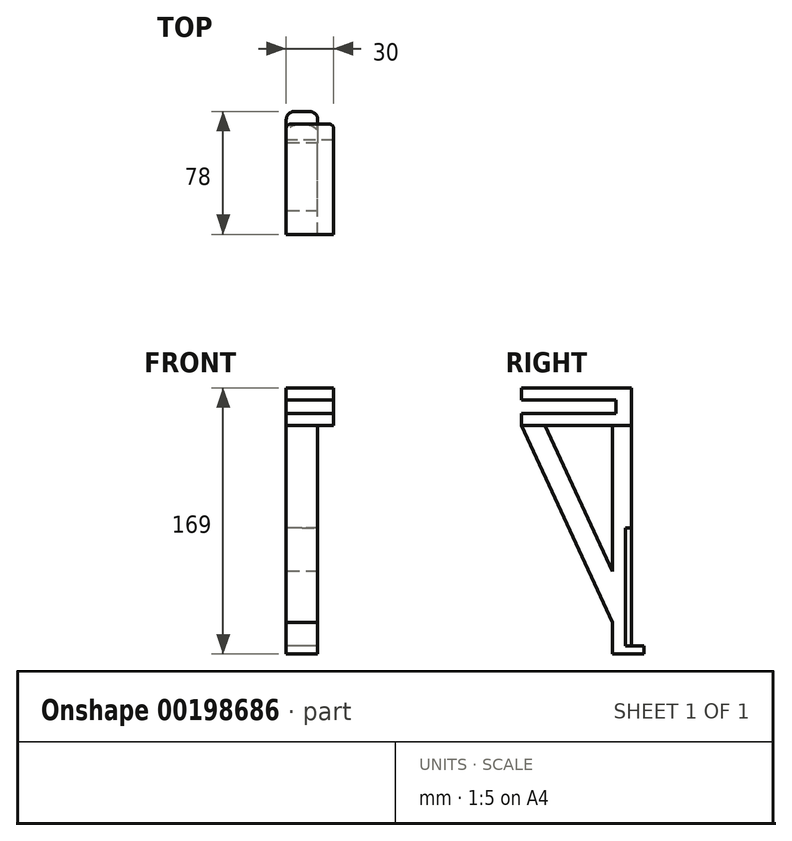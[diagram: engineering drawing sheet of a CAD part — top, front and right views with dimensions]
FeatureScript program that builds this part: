
annotation { "Feature Type Name" : "Feature", "Feature Type Description" : "" }
export const myFeature = defineFeature(function(context is Context, id is Id, definition is map)
    precondition{}
    {
        {
            var Q0;
            Q0=qCreatedBy(makeId("Top.planeOp"),FACE);
            var sketch = newSketch(context, id + "F0", { "sketchPlane" : qUnion([Q0])});
            skLineSegment(sketch, "E0.bottom", {"start": v(0, 0) * mm, "end": v(30, 0) * mm});
            skLineSegment(sketch, "E0.top", {"start": v(0, -70) * mm, "end": v(30, -70) * mm});
            skLineSegment(sketch, "E0.left", {"start": v(0, 0) * mm, "end": v(0, -70) * mm});
            skLineSegment(sketch, "E0.right", {"start": v(30, 0) * mm, "end": v(30, -70) * mm});
            skSolve(sketch);
        }
        {
            var Q0;
            Q0=makeQuery(id+"F0.imprint","IMPRINT",FACE,{"disambiguationData":[TD([[makeQuery(id+"F0.imprint","IMPRINT",EDGE,{"derivedFrom":sQuery(id+"F0.wireOp",EDGE,"E0.bottom")}),-1.0]])]});
            extrude(context, id + "F1", {"entities" : qUnion([Q0]), "depth" : 24 * mm});
        }
        {
            var Q0;
            Q0=makeQuery(id+"F1.opExtrude","SWEPT_FACE",FACE,{"disambiguationData":[OSD([sQuery(id+"F0.wireOp",EDGE,"E0.left")])]});
            var sketch = newSketch(context, id + "F2", { "sketchPlane" : qUnion([Q0])});
            skLineSegment(sketch, "E1.bottom", {"start": v(70, 7.9) * mm, "end": v(10, 7.9) * mm});
            skLineSegment(sketch, "E1.top", {"start": v(70, 16.3) * mm, "end": v(10, 16.3) * mm});
            skLineSegment(sketch, "E1.left", {"start": v(70, 7.9) * mm, "end": v(70, 16.3) * mm});
            skLineSegment(sketch, "E1.right", {"start": v(10, 7.9) * mm, "end": v(10, 16.3) * mm});
            skSolve(sketch);
        }
        {
            var Q0;
            Q0=makeQuery(id+"F2.imprint","IMPRINT",FACE,{"disambiguationData":[TD([[makeQuery(id+"F2.imprint","IMPRINT",EDGE,{"derivedFrom":sQuery(id+"F2.wireOp",EDGE,"E1.bottom")}),-1.0]])]});
            extrude(context, id + "F3", {"entities" : qUnion([Q0]), "operationType" : NewBodyOperationType.REMOVE, "endBound" : BoundingType.THROUGH_ALL, "oppositeDirection" : true, "depth" : 25 * mm});
        }
        {
            var Q0;
            Q0=qCreatedBy(makeId("Right.planeOp"),FACE);
            var sketch = newSketch(context, id + "F4", { "sketchPlane" : qUnion([Q0])});
            skLineSegment(sketch, "E2.bottom", {"start": v(0, 0) * mm, "end": v(-12, 0) * mm});
            skLineSegment(sketch, "E2.top", {"start": v(0, -145) * mm, "end": v(-12, -145) * mm});
            skLineSegment(sketch, "E2.left", {"start": v(0, 0) * mm, "end": v(0, -145) * mm});
            skLineSegment(sketch, "E2.right", {"start": v(-12, 0) * mm, "end": v(-12, -145) * mm});
            skLineSegment(sketch, "E3", {"start": v(-70, 0) * mm, "end": v(-55, 0) * mm});
            skLineSegment(sketch, "E4", {"start": v(-55, 0) * mm, "end": v(-12, -92.67) * mm});
            skLineSegment(sketch, "E5", {"start": v(-70, 0) * mm, "end": v(-12, -125) * mm});
            skSolve(sketch);
        }
        {
            var Q0;
            {var subQ1=sQuery(id+"F4.wireOp",EDGE,"E2.bottom");Q0=makeQuery(id+"F4.imprint","IMPRINT",FACE,{"disambiguationData":[TD([[makeQuery(id+"F4.imprint","IMPRINT",EDGE,{"derivedFrom":subQ1}),1.0]])]});}
            var Q1;
            Q1=makeQuery(id+"F4.imprint","IMPRINT",FACE,{"disambiguationData":[TD([[makeQuery(id+"F4.imprint","IMPRINT",EDGE,{"derivedFrom":sQuery(id+"F4.wireOp",EDGE,"E3")}),-1.0]])]});
            extrude(context, id + "F5", {"entities" : qUnion([Q0, Q1]), "operationType" : NewBodyOperationType.ADD, "depth" : 20 * mm});
        }
        {
            var Q0;
            Q0=makeQuery(id+"F5.boolean.opBoolean","MERGE",FACE,{"derivedFrom":[makeQuery(id+"F1.opExtrude","SWEPT_FACE",FACE,{"disambiguationData":[OSD([sQuery(id+"F0.wireOp",EDGE,"E0.bottom")])]}),makeQuery(id+"F5.opExtrude","SWEPT_FACE",FACE,{"disambiguationData":[OSD([sQuery(id+"F4.wireOp",EDGE,"E2.left")])]})]});
            var sketch = newSketch(context, id + "F6", { "sketchPlane" : qUnion([Q0])});
            skLineSegment(sketch, "E6.bottom", {"start": v(-20, -145) * mm, "end": v(0, -145) * mm});
            skLineSegment(sketch, "E6.top", {"start": v(-20, -140) * mm, "end": v(0, -140) * mm});
            skLineSegment(sketch, "E6.left", {"start": v(-20, -145) * mm, "end": v(-20, -140) * mm});
            skLineSegment(sketch, "E6.right", {"start": v(0, -145) * mm, "end": v(0, -140) * mm});
            skSolve(sketch);
        }
        {
            var Q0;
            Q0=makeQuery(id+"F6.imprint","IMPRINT",FACE,{"disambiguationData":[TD([[makeQuery(id+"F6.imprint","IMPRINT",EDGE,{"derivedFrom":sQuery(id+"F6.wireOp",EDGE,"E6.bottom")}),1.0]])]});
            extrude(context, id + "F7", {"entities" : qUnion([Q0]), "operationType" : NewBodyOperationType.ADD, "depth" : 8 * mm});
        }
        {
            var Q0;
            Q0=makeQuery(id+"F7.opExtrude","SWEPT_FACE",FACE,{"disambiguationData":[OSD([sQuery(id+"F6.wireOp",EDGE,"E6.top")])]});
            var sketch = newSketch(context, id + "F8", { "sketchPlane" : qUnion([Q0])});
            skArc(sketch, "E7", {"start": v(20.46, -4.25) * mm, "mid": v(10.31, 0) * mm, "end": v(0, -3.82) * mm});
            skLineSegment(sketch, "E8.0", {"start": v(20, 0) * mm, "end": v(0, 0) * mm});
            skLineSegment(sketch, "E9.bottom", {"start": v(0, 0) * mm, "end": v(20.46, 0) * mm});
            skLineSegment(sketch, "E9.left", {"start": v(0, 0) * mm, "end": v(0, -3.82) * mm});
            skLineSegment(sketch, "E9.right", {"start": v(20.46, 0) * mm, "end": v(20.46, -4.25) * mm});
            skSolve(sketch);
        }
        {
            var Q0;
            Q0 = qSketchRegion(id + "F8", true);
            extrude(context, id + "F9", {"entities" : qUnion([Q0]), "operationType" : NewBodyOperationType.REMOVE, "depth" : 75 * mm});
        }
        {
            var Q0;
            Q0=makeQuery(id+"F7.opExtrude","CAP_EDGE",EDGE,{"disambiguationData":[OSD([sQuery(id+"F6.wireOp",EDGE,"E6.right")])],"isStart":false});
            var Q1;
            Q1=makeQuery(id+"F7.opExtrude","CAP_EDGE",EDGE,{"disambiguationData":[OSD([sQuery(id+"F6.wireOp",EDGE,"E6.left")])],"isStart":false});
            fillet(context, id + "F10", {"entities" : qUnion([Q0, Q1]), "radius" : 5 * mm, "tangentPropagation" : true, "allowEdgeOverflow" : false});
        }
        {
            var Q0;
            Q0=makeQuery(id+"F5.boolean.opBoolean","MERGE",EDGE,{"derivedFrom":[makeQuery(id+"F1.opExtrude","SWEPT_EDGE",EDGE,{"disambiguationData":[OSD([sQuery(id+"F0.wireOp",EDGE,"E0.bottom"),sQuery(id+"F0.wireOp",EDGE,"E0.left")])]}),makeQuery(id+"F5.opExtrude","CAP_EDGE",EDGE,{"disambiguationData":[OSD([sQuery(id+"F4.wireOp",EDGE,"E2.left")])],"isStart":true})]});
            var Q1;
            Q1=makeQuery(id+"F5.opExtrude","CAP_EDGE",EDGE,{"disambiguationData":[OSD([sQuery(id+"F4.wireOp",EDGE,"E2.left")])],"isStart":false});
            fillet(context, id + "F11", {"entities" : qUnion([Q0, Q1]), "radius" : 2.5 * mm, "tangentPropagation" : true, "allowEdgeOverflow" : false});
        }
        {
            var Q0;
            Q0=makeQuery(id+"F1.opExtrude","SWEPT_EDGE",EDGE,{"disambiguationData":[OSD([sQuery(id+"F0.wireOp",EDGE,"E0.bottom"),sQuery(id+"F0.wireOp",EDGE,"E0.right")])]});
            fillet(context, id + "F12", {"entities" : qUnion([Q0]), "radius" : 2.5 * mm, "tangentPropagation" : true, "allowEdgeOverflow" : false});
        }
    });
